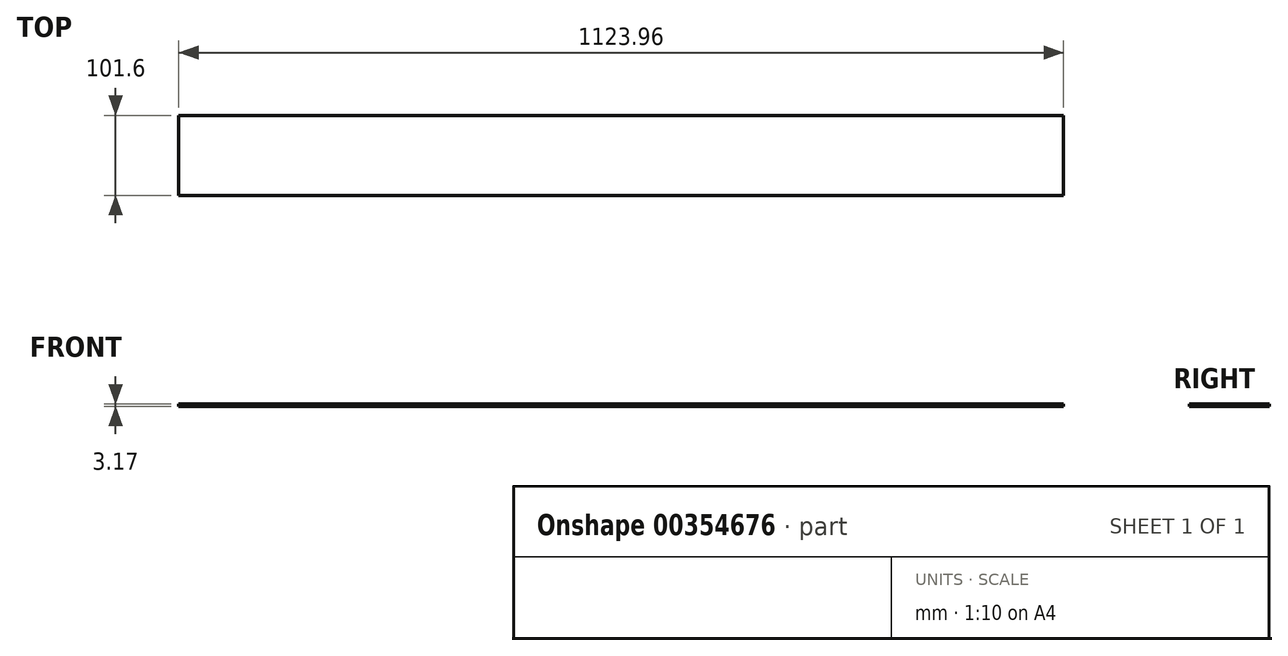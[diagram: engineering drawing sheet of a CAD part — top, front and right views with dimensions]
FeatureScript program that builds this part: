
annotation { "Feature Type Name" : "Feature", "Feature Type Description" : "" }
export const myFeature = defineFeature(function(context is Context, id is Id, definition is map)
    precondition{}
    {
        {
            var Q0;
            Q0=qCreatedBy(makeId("Top.planeOp"),FACE);
            var sketch = newSketch(context, id + "F0", { "sketchPlane" : qUnion([Q0])});
            skLineSegment(sketch, "E0.bottom", {"start": v(561.98, 50.8) * mm, "end": v(-561.98, 50.8) * mm});
            skLineSegment(sketch, "E0.top", {"start": v(561.98, -50.8) * mm, "end": v(-561.98, -50.8) * mm});
            skLineSegment(sketch, "E0.left", {"start": v(561.98, 50.8) * mm, "end": v(561.98, -50.8) * mm});
            skLineSegment(sketch, "E0.right", {"start": v(-561.98, 50.8) * mm, "end": v(-561.98, -50.8) * mm});
            skPoint(sketch, "E0.middle", {"position": v(0, 0) * mm});
            skSolve(sketch);
        }
        {
            var Q0;
            Q0=qSketchRegion(id+"F0",true);
            extrude(context, id + "F1", {"entities" : qUnion([Q0]), "depth" : 3.17 * mm});
        }
    });
